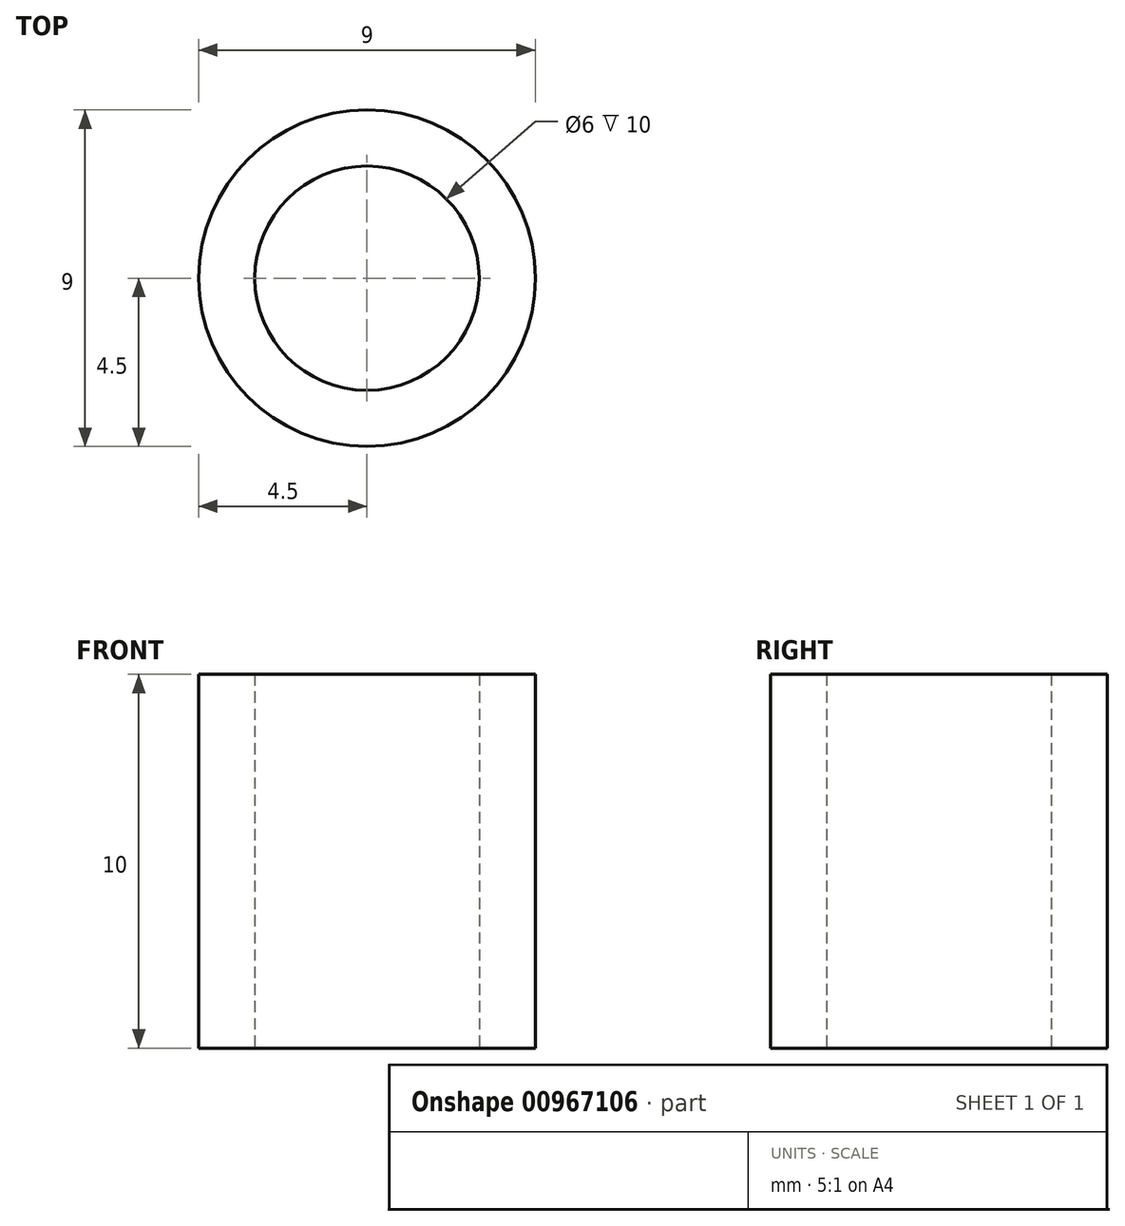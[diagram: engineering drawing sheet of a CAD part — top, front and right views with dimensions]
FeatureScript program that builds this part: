
annotation { "Feature Type Name" : "Feature", "Feature Type Description" : "" }
export const myFeature = defineFeature(function(context is Context, id is Id, definition is map)
    precondition{}
    {
        {
            var Q0;
            Q0=qCreatedBy(makeId("Top.planeOp"),FACE);
            var sketch = newSketch(context, id + "F0", { "sketchPlane" : qUnion([Q0])});
            skCircle(sketch, "E0", {"center": v(0, 0) * mm, "radius": 4.5 * mm});
            skCircle(sketch, "E1", {"center": v(0, 0) * mm, "radius": 3 * mm});
            skSolve(sketch);
        }
        {
            var Q0;
            Q0=makeQuery(id+"F0.imprint","IMPRINT",FACE,{"disambiguationData":[TD([[makeQuery(id+"F0.imprint","IMPRINT",EDGE,{"derivedFrom":sQuery(id+"F0.wireOp",EDGE,"E0")}),1.0]])]});
            extrude(context, id + "F1", {"entities" : qUnion([Q0]), "depth" : 10 * mm, "offsetDistance" : 25 * mm});
        }
    });
